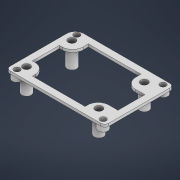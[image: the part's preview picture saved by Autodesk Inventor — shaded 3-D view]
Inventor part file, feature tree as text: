
AUTODESK INVENTOR PART (.ipt)
format: ipt  version: 2021 (Build 250183000, 183)  size: 489,984 bytes
history: native  units: mm
features: extrude x7, sketch x7, fillet x3, projected_geometry x1
ambient origin geometry x8: Origin, YZ Plane, XZ Plane, XY Plane, X Axis, Y Axis, Z Axis, Center Point
bodies: Volumenkörper1 (feature_tree)
feature tree (18):
  extrude  "Extrusion1"  Depth=52.5mm
  extrude  "Extrusion2"  Depth=2.0mm
  sketch  "Skizze5"  dims[d12=17.25mm d13=17.25mm]
  extrude  "Extrusion5"  Depth=7.0mm
  extrude  "Extrusion6"  Depth=34.5mm
  extrude  "Extrusion3"  Depth=17.25mm
  extrude  "Extrusion4"  Depth=55.0mm
  extrude  "Extrusion7"  Depth=3.0mm
  fillet  "Rundung1"  Radius=55.0mm
  fillet  "Rundung2"  Radius=15.0mm
  fillet  "Rundung3"  Radius=5.5mm
  sketch  "Skizze1"  dims[d0=75.0mm d1=52.5mm]
  sketch  "Skizze2"  dims[d2=2.0mm d3=0.0mm d4=7.0mm]
  sketch  "Skizze3"  dims[d5=7.0mm d6=7.0mm]
  sketch  "Skizze4"  dims[d7=7.0mm d8=34.5mm]
  projected_geometry  "Projizierte Kontur1"
  sketch  "Skizze6"  dims[d14=34.5mm d15=55.0mm]
  sketch  "Skizze7"  dims[d16=31.0mm d17=31.0mm d18=55.0mm d19=15.0mm d20=0.0mm d21=5.5mm d22=5.5mm d23=5.5mm d24=5.5mm d25=4.0mm d26=0.0mm d27=3.2mm d28=3.2mm d29=3.2mm d30=3.2mm d31=4.0mm d32=0.0mm d33=7.0mm d34=7.0mm d35=7.0mm d36=7.0mm d39=65.5mm d40=4.75mm d42=45.5mm d44=65.5mm d45=4.5mm d46=4.5mm d47=4.5mm d48=4.5mm d50=7.0mm d53=7.0mm d56=7.0mm d59=7.0mm d62=4.0mm d63=0.0mm d64=6.0mm d65=0.0mm d66=22.75mm d67=32.75mm d68=32.75mm d69=22.75mm d70=32.75mm d71=22.75mm d72=32.75mm d73=32.75mm d74=22.75mm d75=32.75mm d76=22.75mm d77=5.0mm d78=5.0mm d79=15.0mm d80=15.0mm d83=5.0mm d84=15.0mm d86=17.0mm d87=17.0mm d88=5.0mm d89=5.0mm d93=17.0mm d94=5.0mm d95=17.0mm d96=20.0mm d97=20.0mm d98=5.0mm d99=15.0mm d100=6.0mm d101=0.0mm d102=8.0mm d103=3.5mm d104=6.5mm d105=3.0mm]
